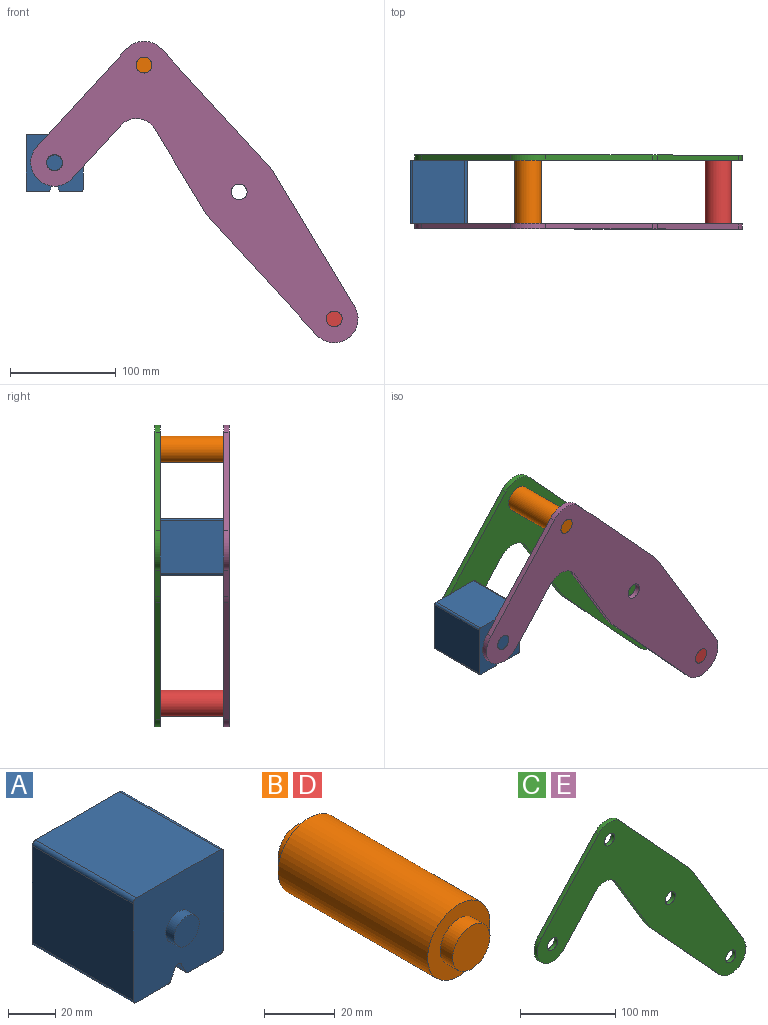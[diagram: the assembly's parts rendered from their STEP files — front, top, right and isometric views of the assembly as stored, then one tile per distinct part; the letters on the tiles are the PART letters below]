
ASSEMBLY  parts=5 mates=3
PART A: 20 faces, bbox 54x70x54 mm
  f0: plane 60x50.01mm, normal (-1,0,0), area 3000.4mm2, adj f7,f10,f13,f19
  f1: plane 60x50.01mm, normal (0,0,1), area 3000.4mm2, adj f7,f10,f13,f14
  f2: plane 60x50.01mm, normal (1,0,0), area 3000.4mm2, adj f7,f10,f14,f15
  f3: plane 60x18.77mm, normal (0,0,-1), area 1126mm2, adj f7,f10,f15,f16
  f4: plane 60x5.32mm, normal (-0.89,0,-0.45), area 356.7mm2, adj f7,f10,f16,f17
  f5: plane 60x5.32mm, normal (0.89,0,-0.45), area 356.7mm2, adj f7,f10,f17,f18
  f6: plane 60x18.77mm, normal (0,0,-1), area 1126mm2, adj f7,f10,f18,f19
  f7: plane 54.01x54.01mm, normal (0,-1,0), area 2689.6mm2, adj f0,f1,f2,f3,f4,f5,f6,f9
  f8: plane 15x15mm, normal (0,-1,0), area 176.7mm2, adj f9
  f9: cylinder r=7.5mm len=15mm, axis (0,1,0), area 235.6mm2, adj f7,f8
  f10: plane 54.01x54.01mm, normal (0,1,0), area 2689.6mm2, adj f0,f1,f2,f3,f4,f5,f6,f12
  f11: plane 15x15mm, normal (0,1,0), area 176.7mm2, adj f12
  f12: cylinder r=7.5mm len=15mm, axis (0,-1,0), area 235.6mm2, adj f10,f11
  f13: cylinder r=2mm len=60mm, axis (0,-1,0), area 188.5mm2, adj f0,f1,f7,f10
  f14: cylinder r=2mm len=60mm, axis (0,1,0), area 188.5mm2, adj f1,f2,f7,f10
  f15: cylinder r=2mm len=60mm, axis (0,-1,0), area 188.5mm2, adj f2,f3,f7,f10
  f16: cylinder r=2mm len=60mm, axis (0,-1,0), area 132.9mm2, adj f3,f4,f7,f10
  f17: cylinder r=2mm len=60mm, axis (0,-1,0), area 265.7mm2, adj f4,f5,f7,f10
  f18: cylinder r=2mm len=60mm, axis (0,1,0), area 132.9mm2, adj f5,f6,f7,f10
  f19: cylinder r=2mm len=60mm, axis (0,1,0), area 188.5mm2, adj f0,f6,f7,f10
PART B: 7 faces, bbox 25x70x25 mm
  f0: cylinder r=12.5mm len=60mm, axis (0,-1,0), area 4712.4mm2, adj f2,f5
  f1: cylinder r=7.5mm len=15mm, axis (0,1,0), area 235.6mm2, adj f2,f3
  f2: plane 25x25mm, normal (0,-1,0), area 314.2mm2, adj f0,f1
  f3: plane 15x15mm, normal (0,-1,0), area 176.7mm2, adj f1
  f4: cylinder r=7.5mm len=15mm, axis (0,-1,0), area 235.6mm2, adj f5,f6
  f5: plane 25x25mm, normal (0,1,0), area 314.2mm2, adj f0,f4
  f6: plane 15x15mm, normal (0,1,0), area 176.7mm2, adj f4
PART C: 18 faces, bbox 309.5x5x285.1 mm
  f0: cylinder r=22.5mm len=39.07mm, axis (0,1,0), area 353.4mm2, adj f1,f13,f16,f17
  f1: plane 50.28x46.21mm, normal (0.74,0,-0.68), area 341.4mm2, adj f0,f2,f16,f17
  f2: cylinder r=20mm len=31.85mm, axis (0,1,0), area 185.5mm2, adj f1,f3,f16,f17
  f3: plane 79.23x47.81mm, normal (-0.86,0,-0.52), area 462.7mm2, adj f2,f4,f16,f17
  f4: cylinder r=37.5mm len=6mm, axis (0,1,0), area 37.6mm2, adj f3,f5,f16,f17
  f5: plane 109.88x101mm, normal (-0.74,0,-0.68), area 746.2mm2, adj f4,f6,f16,f17
  f6: cylinder r=22.5mm len=39.07mm, axis (0,1,0), area 330.9mm2, adj f5,f7,f16,f17
  f7: plane 127.78x77.11mm, normal (0.86,0,0.52), area 746.2mm2, adj f6,f8,f16,f17
  f8: cylinder r=37.5mm len=6mm, axis (0,1,0), area 37.6mm2, adj f7,f9,f16,f17
  f9: plane 109.88x101mm, normal (0.74,0,0.68), area 746.2mm2, adj f8,f10,f16,f17
  f10: cylinder r=22.5mm len=33.13mm, axis (0,1,0), area 186.2mm2, adj f9,f13,f16,f17
  f11: cylinder r=7.5mm len=15mm, axis (0,1,0), area 235.6mm2, adj f16,f17
  f12: cylinder r=7.5mm len=15mm, axis (0,1,0), area 235.6mm2, adj f16,f17
  f13: plane 92.03x84.59mm, normal (-0.74,0,0.68), area 625mm2, adj f0,f10,f16,f17
  f14: cylinder r=7.5mm len=15mm, axis (0,1,0), area 235.6mm2, adj f16,f17
  f15: cylinder r=7.5mm len=15mm, axis (0,1,0), area 235.6mm2, adj f16,f17
  f16: plane 309.5x285.07mm, normal (0,-1,0), area 24555.4mm2, adj f0,f1,f2,f3,f4,f5,f6,f7
  f17: plane 309.5x285.07mm, normal (0,1,0), area 24555.4mm2, adj f0,f1,f2,f3,f4,f5,f6,f7
PART D: same geometry as B
PART E: same geometry as C
PLACE A t=(-49.1,-101.68,48.76)mm
PLACE B t=(-49.1,-101.68,49.18)mm
PLACE C t=(-49.1,-36.68,49.18)mm
PLACE D t=(130.81,-101.68,-190.89)mm
PLACE E t=(-49.1,-101.68,49.18)mm fixed
MATE revolute E.f0 <-> A.f7  axis (0,1,0) through (-223.65,-101.68,77.18)mm
MATE fastened B.f0 <-> C.f10  axis (0,-1,0) through (-139.06,-41.68,169.21)mm
MATE fastened E.f6 <-> D.f0  axis (0,1,0) through (40.85,-101.68,-70.86)mm
